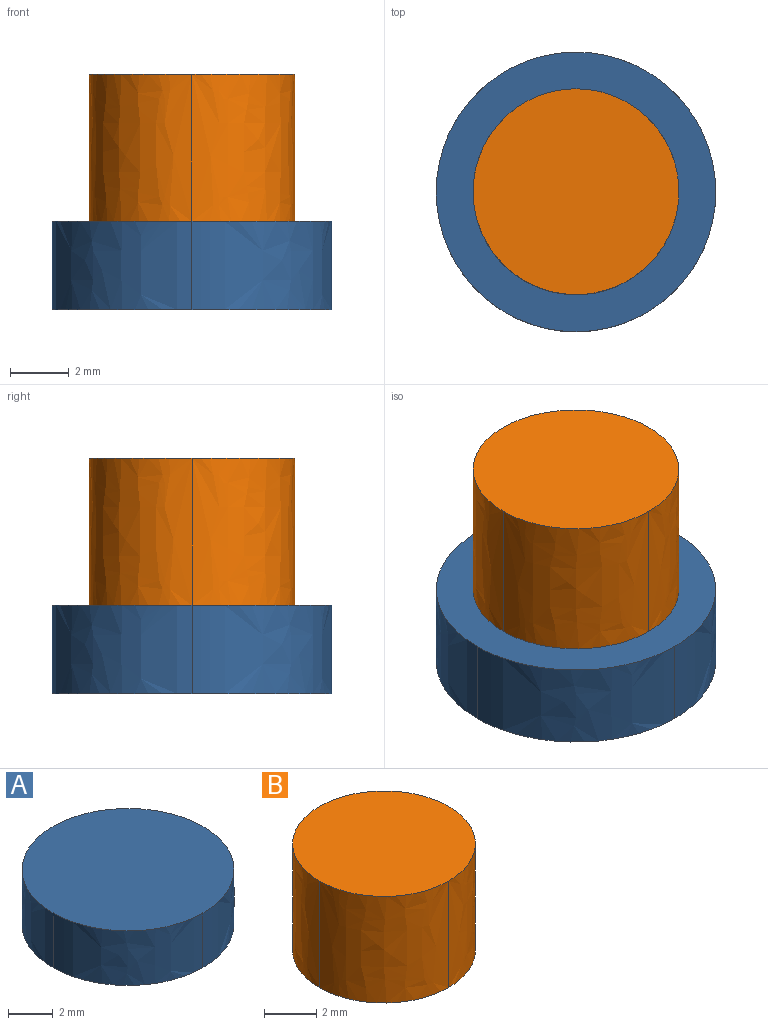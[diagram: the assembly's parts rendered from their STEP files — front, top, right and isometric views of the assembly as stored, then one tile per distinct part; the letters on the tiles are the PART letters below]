
ASSEMBLY  parts=2 mates=1
PART A: 6 faces, bbox 9.5x9.5x3 mm
  f0: extruded ~4.75x4.75mm, area 22.4mm2, adj f1,f3,f4,f5
  f1: extruded ~4.75x4.75mm, area 22.4mm2, adj f0,f2,f4,f5
  f2: extruded ~4.75x4.75mm, area 22.4mm2, adj f1,f3,f4,f5
  f3: extruded ~4.75x4.75mm, area 22.4mm2, adj f0,f2,f4,f5
  f4: plane 9.51x9.51mm, normal (0,0,1), area 71mm2, adj f0,f1,f2,f3
  f5: plane 9.51x9.51mm, normal (0,0,-1), area 71mm2, adj f0,f1,f2,f3
PART B: 6 faces, bbox 7x7x5 mm
  f0: extruded ~5x3.5mm, area 27.5mm2, adj f1,f3,f4,f5
  f1: extruded ~5x3.5mm, area 27.5mm2, adj f0,f2,f4,f5
  f2: extruded ~5x3.5mm, area 27.5mm2, adj f1,f3,f4,f5
  f3: extruded ~5x3.5mm, area 27.5mm2, adj f0,f2,f4,f5
  f4: plane 7x7mm, normal (0,0,1), area 38.5mm2, adj f0,f1,f2,f3
  f5: plane 7x7mm, normal (0,0,-1), area 38.5mm2, adj f0,f1,f2,f3
PLACE A t=(-82.53,-19.82,0)mm
PLACE B t=(-47.4,25.41,3)mm
MATE fastened B.f5 <-> A.f4  axis (0,0,-1) through (0,0,3)mm
